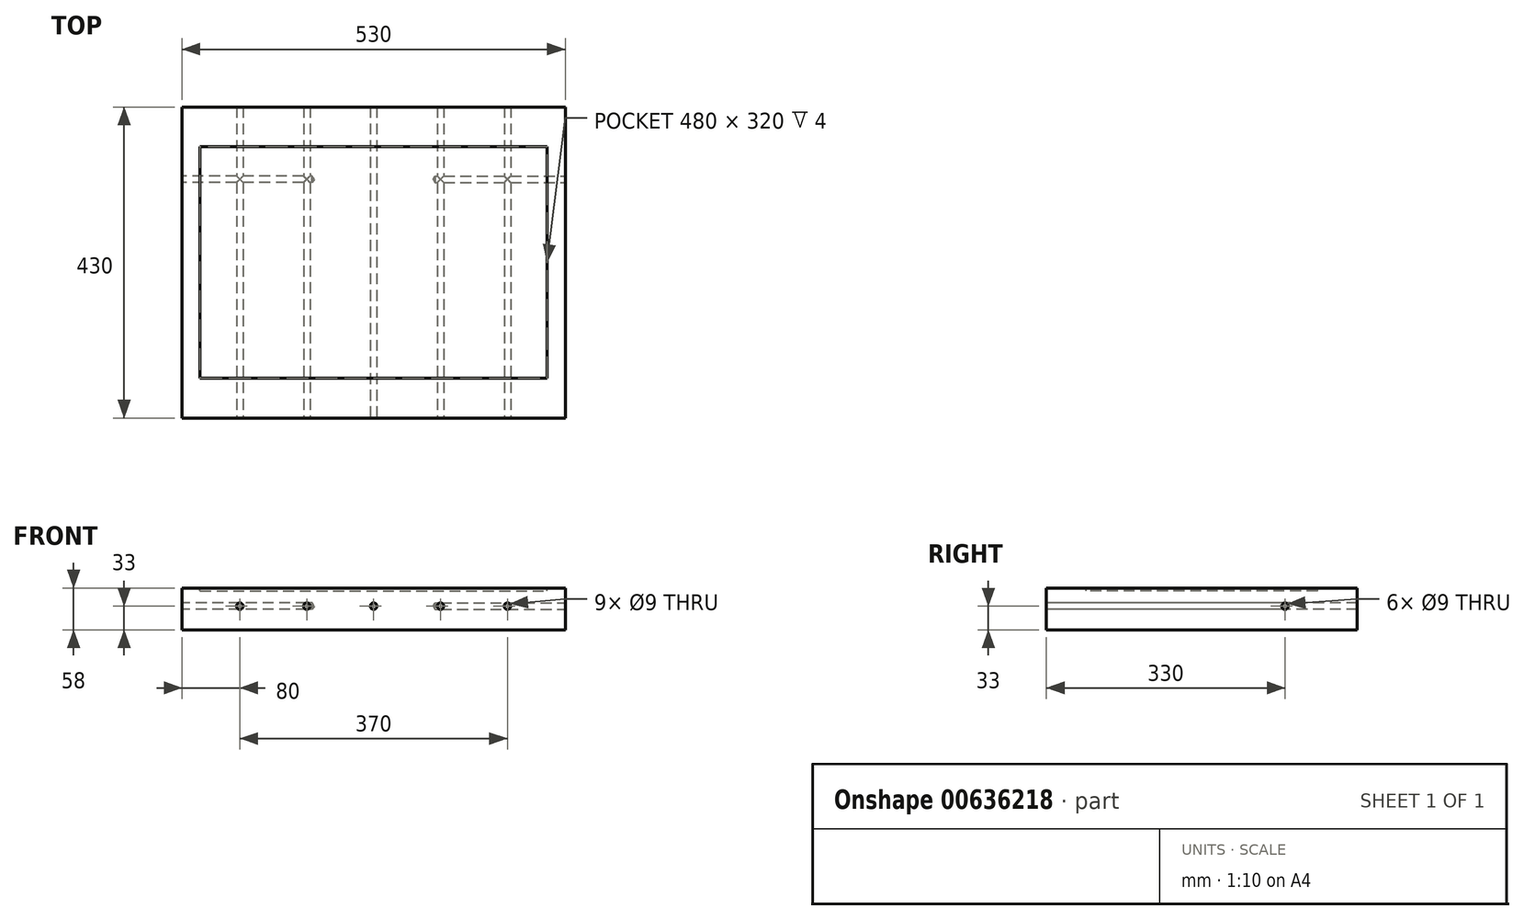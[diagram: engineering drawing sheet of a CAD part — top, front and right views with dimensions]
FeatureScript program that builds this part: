
annotation { "Feature Type Name" : "Feature", "Feature Type Description" : "" }
export const myFeature = defineFeature(function(context is Context, id is Id, definition is map)
    precondition{}
    {
        {
            var Q0;
            Q0=qCreatedBy(makeId("Top.planeOp"),FACE);
            var sketch = newSketch(context, id + "F0", { "sketchPlane" : qUnion([Q0])});
            skLineSegment(sketch, "E0.bottom", {"start": v(-530, 430) * mm, "end": v(0, 430) * mm});
            skLineSegment(sketch, "E0.top", {"start": v(-530, 0) * mm, "end": v(0, 0) * mm});
            skLineSegment(sketch, "E0.left", {"start": v(-530, 430) * mm, "end": v(-530, 0) * mm});
            skLineSegment(sketch, "E0.right", {"start": v(0, 430) * mm, "end": v(0, 0) * mm});
            skSolve(sketch);
        }
        {
            var Q0;
            Q0=makeQuery(id+"F0.imprint","IMPRINT",FACE,{"disambiguationData":[TD([[makeQuery(id+"F0.imprint","IMPRINT",EDGE,{"derivedFrom":sQuery(id+"F0.wireOp",EDGE,"E0.bottom")}),-1.0]])]});
            extrude(context, id + "F1", {"entities" : qUnion([Q0]), "depth" : 58 * mm, "offsetDistance" : 25 * mm});
        }
        {
            var Q0;
            Q0=makeQuery(id+"F1.opExtrude","SWEPT_FACE",FACE,{"disambiguationData":[OSD([sQuery(id+"F0.wireOp",EDGE,"E0.top")])]});
            var sketch = newSketch(context, id + "F2", { "sketchPlane" : qUnion([Q0])});
            skCircle(sketch, "E1", {"center": v(-450, 33) * mm, "radius": 3.2 * mm});
            skCircle(sketch, "E2.1.0.0", {"center": v(-357.5, 33) * mm, "radius": 3.2 * mm});
            skCircle(sketch, "E2.2.0.0", {"center": v(-265, 33) * mm, "radius": 3.2 * mm});
            skCircle(sketch, "E2.3.0.0", {"center": v(-172.5, 33) * mm, "radius": 3.2 * mm});
            skCircle(sketch, "E2.4.0.0", {"center": v(-80, 33) * mm, "radius": 3.2 * mm});
            skLineSegment(sketch, "E2.direction1", {"start": v(-450, 33) * mm, "end": v(-357.5, 33) * mm, "construction": true});
            skSolve(sketch);
        }
        {
            var Q0;
            Q0=sQuery(id+"F2.wireOp",VERTEX,"E2.direction1.start");
            var Q1;
            Q1=sQuery(id+"F2.wireOp",VERTEX,"E2.direction1.end");
            var Q2;
            Q2=sQuery(id+"F2.wireOp",VERTEX,"E2.2.0.0.center");
            var Q3;
            Q3=sQuery(id+"F2.wireOp",VERTEX,"E2.3.0.0.center");
            var Q4;
            Q4=sQuery(id+"F2.wireOp",VERTEX,"E2.4.0.0.center");
            var Q5;
            Q5=sQuery(id+"F2.wireOp",VERTEX,"E2.5.0.0.center");
            var Q6;
            Q6=makeQuery(id+"F1.opExtrude","SWEPT_BODY",BODY,{"disambiguationData":[OSD([sQuery(id+"F0.wireOp",EDGE,"E0.bottom"),sQuery(id+"F0.wireOp",EDGE,"E0.top"),sQuery(id+"F0.wireOp",EDGE,"E0.left"),sQuery(id+"F0.wireOp",EDGE,"E0.right")])]});
            hole(context, id + "F3", {"style" : HoleStyle.SIMPLE, "endStyle" : HoleEndStyle.THROUGH, "standardTappedOrClearance" : lookupTablePath({ "fit" : "Normal", "standard" : "ISO", "size" : "M8", "type" : "Clearance" }), "standardBlindInLast" : lookupTablePath({ "fit" : "Normal", "standard" : "ISO", "engagement" : "75%", "pitch" : "1.25 mm", "size" : "M8", "type" : "Clearance & tapped" }), "holeDiameter" : 9 * mm, "majorDiameter" : 5 * mm, "isTappedThrough" : true, "tappedDepth" : 7 * mm, "tapClearance" : 3, "startFromSketch" : true, "locations" : qUnion([Q0, Q1, Q2, Q3, Q4, Q5]), "scope" : qUnion([Q6])});
        }
        {
            var Q0;
            Q0=makeQuery(id+"F1.opExtrude","SWEPT_FACE",FACE,{"disambiguationData":[OSD([sQuery(id+"F0.wireOp",EDGE,"E0.left")])]});
            var sketch = newSketch(context, id + "F4", { "sketchPlane" : qUnion([Q0])});
            skPoint(sketch, "E3", {"position": v(-330, 33) * mm});
            skSolve(sketch);
        }
        {
            var Q0;
            Q0=sQuery(id+"F4.wireOp",VERTEX,"E3");
            var Q1;
            Q1=makeQuery(id+"F1.opExtrude","SWEPT_BODY",BODY,{"disambiguationData":[OSD([sQuery(id+"F0.wireOp",EDGE,"E0.bottom"),sQuery(id+"F0.wireOp",EDGE,"E0.top"),sQuery(id+"F0.wireOp",EDGE,"E0.left"),sQuery(id+"F0.wireOp",EDGE,"E0.right")])]});
            hole(context, id + "F5", {"style" : HoleStyle.SIMPLE, "endStyle" : HoleEndStyle.BLIND, "standardTappedOrClearance" : lookupTablePath({ "fit" : "Normal", "standard" : "ISO", "size" : "M8", "type" : "Clearance" }), "standardBlindInLast" : lookupTablePath({ "fit" : "Normal", "standard" : "ISO", "engagement" : "75%", "pitch" : "1.25 mm", "size" : "M8", "type" : "Clearance & tapped" }), "holeDiameter" : 9 * mm, "majorDiameter" : 5 * mm, "holeDepth" : 180 * mm, "isTappedThrough" : true, "tappedDepth" : 7 * mm, "tapClearance" : 3, "startFromSketch" : true, "locations" : qUnion([Q0]), "scope" : qUnion([Q1])});
        }
        {
            var Q0;
            Q0=makeQuery(id+"F1.opExtrude","SWEPT_FACE",FACE,{"disambiguationData":[OSD([sQuery(id+"F0.wireOp",EDGE,"E0.right")])]});
            var sketch = newSketch(context, id + "F6", { "sketchPlane" : qUnion([Q0])});
            skPoint(sketch, "E4", {"position": v(330, 33) * mm});
            skSolve(sketch);
        }
        {
            var Q0;
            Q0=sQuery(id+"F6.wireOp",VERTEX,"E4");
            var Q1;
            Q1=makeQuery(id+"F1.opExtrude","SWEPT_BODY",BODY,{"disambiguationData":[OSD([sQuery(id+"F0.wireOp",EDGE,"E0.bottom"),sQuery(id+"F0.wireOp",EDGE,"E0.top"),sQuery(id+"F0.wireOp",EDGE,"E0.left"),sQuery(id+"F0.wireOp",EDGE,"E0.right")])]});
            hole(context, id + "F7", {"style" : HoleStyle.SIMPLE, "endStyle" : HoleEndStyle.BLIND, "standardTappedOrClearance" : lookupTablePath({ "fit" : "Normal", "standard" : "ISO", "size" : "M8", "type" : "Clearance" }), "standardBlindInLast" : lookupTablePath({ "fit" : "Normal", "standard" : "ISO", "engagement" : "75%", "pitch" : "1.25 mm", "size" : "M8", "type" : "Clearance & tapped" }), "holeDiameter" : 9 * mm, "majorDiameter" : 5 * mm, "holeDepth" : 180 * mm, "isTappedThrough" : true, "tappedDepth" : 7 * mm, "tapClearance" : 3, "startFromSketch" : true, "locations" : qUnion([Q0]), "scope" : qUnion([Q1])});
        }
        {
            var Q0;
            Q0=makeQuery(id+"F1.opExtrude","CAP_FACE",FACE,{"disambiguationData":[OSD([sQuery(id+"F0.wireOp",EDGE,"E0.bottom"),sQuery(id+"F0.wireOp",EDGE,"E0.top"),sQuery(id+"F0.wireOp",EDGE,"E0.left"),sQuery(id+"F0.wireOp",EDGE,"E0.right")])],"isStart":false});
            var sketch = newSketch(context, id + "F8", { "sketchPlane" : qUnion([Q0])});
            skLineSegment(sketch, "E5.bottom", {"start": v(-505, 375) * mm, "end": v(-25, 375) * mm});
            skLineSegment(sketch, "E5.top", {"start": v(-505, 55) * mm, "end": v(-25, 55) * mm});
            skLineSegment(sketch, "E5.left", {"start": v(-505, 375) * mm, "end": v(-505, 55) * mm});
            skLineSegment(sketch, "E5.right", {"start": v(-25, 375) * mm, "end": v(-25, 55) * mm});
            skPoint(sketch, "E6.startSnap0", {"position": v(0, 215) * mm});
            skPoint(sketch, "E6.endSnap0", {"position": v(-530, 215) * mm});
            skSolve(sketch);
        }
        {
            var Q0;
            Q0 = qSketchRegion(id + "F8", true);
            extrude(context, id + "F9", {"entities" : qUnion([Q0]), "operationType" : NewBodyOperationType.REMOVE, "oppositeDirection" : true, "depth" : 4 * mm, "offsetDistance" : 25 * mm});
        }
    });
